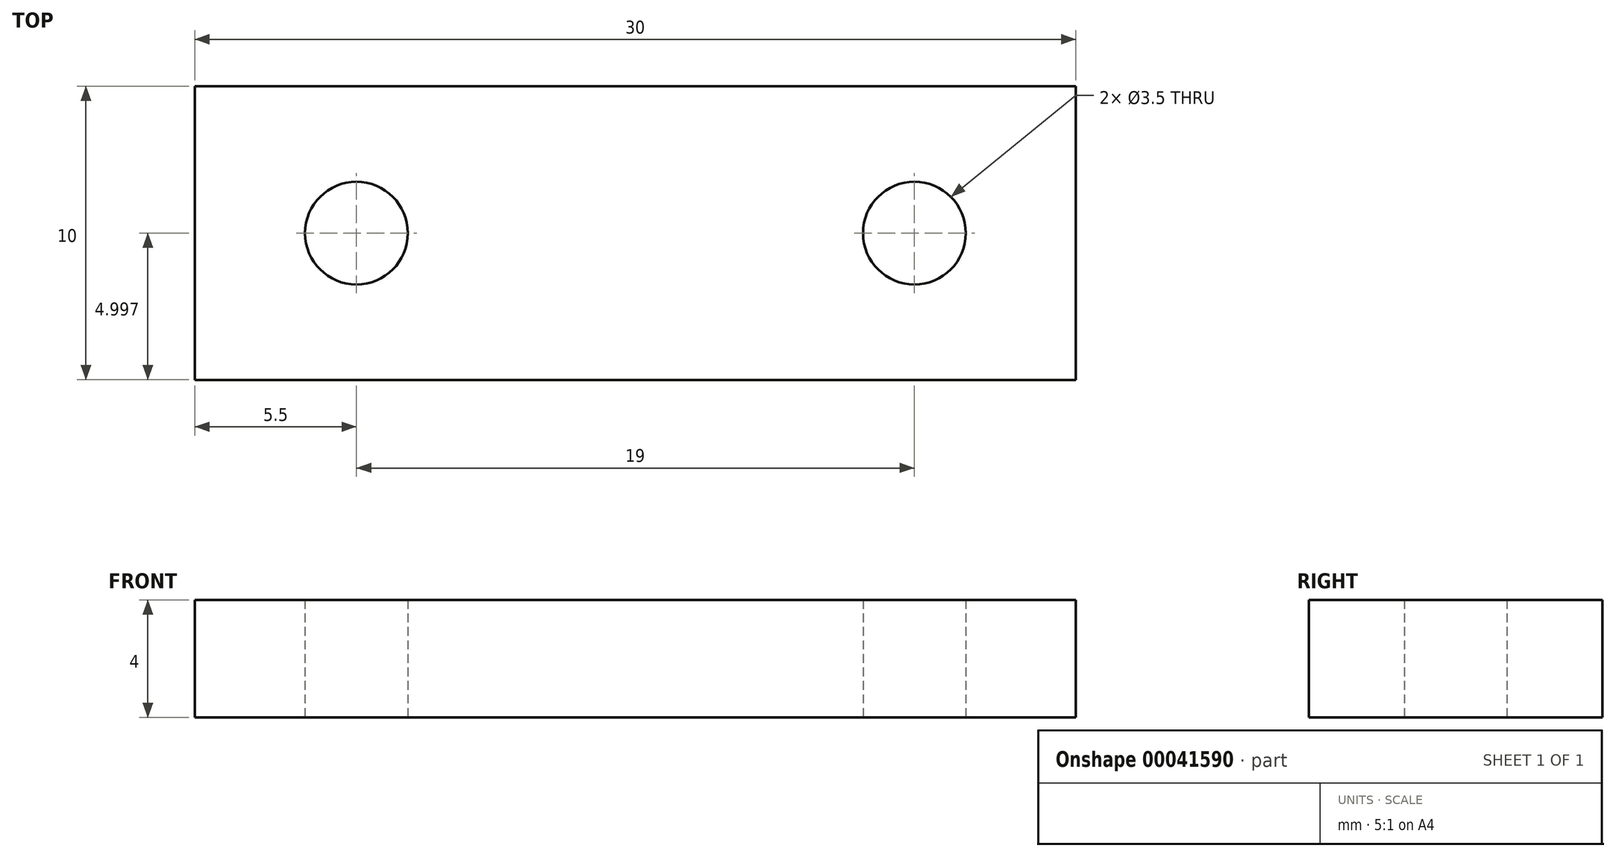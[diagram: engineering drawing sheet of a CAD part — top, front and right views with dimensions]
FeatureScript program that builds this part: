
annotation { "Feature Type Name" : "Feature", "Feature Type Description" : "" }
export const myFeature = defineFeature(function(context is Context, id is Id, definition is map)
    precondition{}
    {
        {
            var Q0;
            Q0=qCreatedBy(makeId("Top.planeOp"),FACE);
            var sketch = newSketch(context, id + "F0", { "sketchPlane" : qUnion([Q0])});
            skCircle(sketch, "E0", {"center": v(-13.63, 29.98) * mm, "radius": 1.75 * mm});
            skCircle(sketch, "E1", {"center": v(5.37, 29.98) * mm, "radius": 1.75 * mm});
            skLineSegment(sketch, "E2.rect.bottom", {"start": v(10.87, 24.98) * mm, "end": v(-19.13, 24.98) * mm});
            skLineSegment(sketch, "E2.rect.top", {"start": v(10.87, 34.98) * mm, "end": v(-19.13, 34.98) * mm});
            skLineSegment(sketch, "E2.rect.left", {"start": v(10.87, 24.98) * mm, "end": v(10.87, 34.98) * mm});
            skLineSegment(sketch, "E2.rect.right", {"start": v(-19.13, 24.98) * mm, "end": v(-19.13, 34.98) * mm});
            skPoint(sketch, "E2.rect.middle", {"position": v(-4.13, 29.98) * mm});
            skSolve(sketch);
        }
        {
            var Q0;
            Q0=makeQuery(id+"F0.imprint","IMPRINT",FACE,{"disambiguationData":[TD([[makeQuery(id+"F0.imprint","IMPRINT",EDGE,{"derivedFrom":sQuery(id+"F0.wireOp",EDGE,"E0")}),-1.0]])]});
            extrude(context, id + "F1", {"entities" : qUnion([Q0]), "depth" : 4 * mm});
        }
    });
